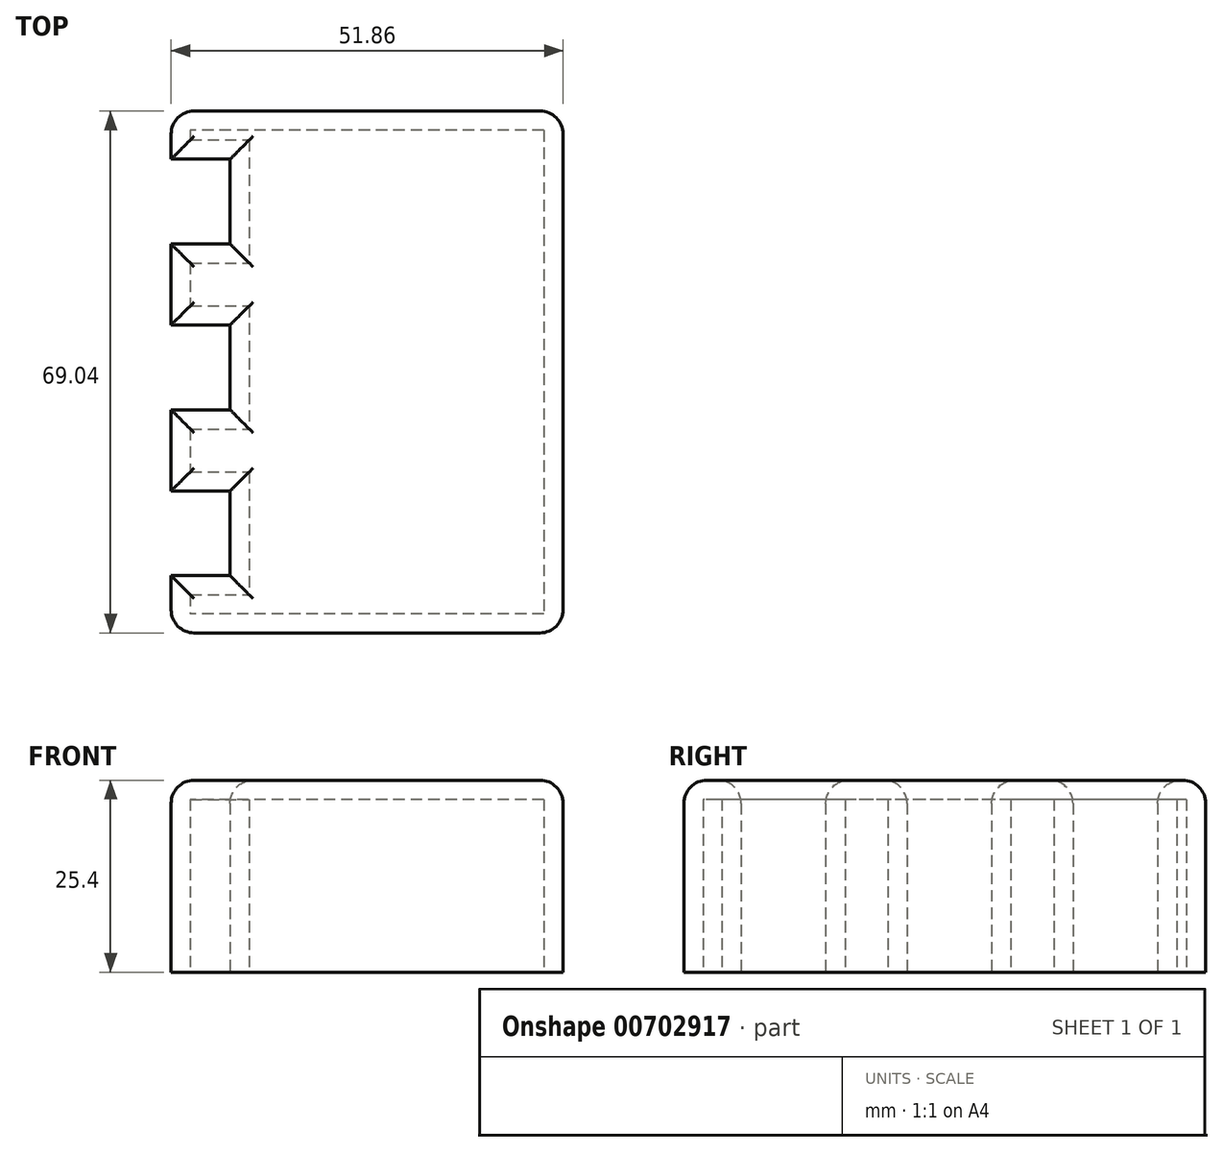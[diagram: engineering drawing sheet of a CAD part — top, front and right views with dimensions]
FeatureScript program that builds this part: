
annotation { "Feature Type Name" : "Feature", "Feature Type Description" : "" }
export const myFeature = defineFeature(function(context is Context, id is Id, definition is map)
    precondition{}
    {
        {
            var Q0;
            Q0=qCreatedBy(makeId("Top.planeOp"),FACE);
            var sketch = newSketch(context, id + "F0", { "sketchPlane" : qUnion([Q0])});
            skLineSegment(sketch, "E0.bottom", {"start": v(25.93, 34.52) * mm, "end": v(-25.93, 34.52) * mm});
            skLineSegment(sketch, "E0.top", {"start": v(25.93, -34.52) * mm, "end": v(-25.93, -34.52) * mm});
            skLineSegment(sketch, "E0.left", {"start": v(25.93, 34.52) * mm, "end": v(25.93, -34.52) * mm});
            skLineSegment(sketch, "E0.right", {"start": v(-25.93, 34.52) * mm, "end": v(-25.93, 28.16) * mm});
            skPoint(sketch, "E0.middle", {"position": v(0, 0) * mm});
            skLineSegment(sketch, "E1.bottom", {"start": v(-25.93, 28.16) * mm, "end": v(-18.13, 28.16) * mm});
            skLineSegment(sketch, "E1.top", {"start": v(-25.93, 16.96) * mm, "end": v(-18.13, 16.96) * mm});
            skLineSegment(sketch, "E1.right", {"start": v(-18.13, 28.16) * mm, "end": v(-18.13, 16.96) * mm});
            skLineSegment(sketch, "E2.bottom", {"start": v(-25.93, 6.2) * mm, "end": v(-18.13, 6.2) * mm});
            skLineSegment(sketch, "E2.top", {"start": v(-25.93, -5) * mm, "end": v(-18.13, -5) * mm});
            skLineSegment(sketch, "E2.right", {"start": v(-18.13, 6.2) * mm, "end": v(-18.13, -5) * mm});
            skLineSegment(sketch, "E3.bottom", {"start": v(-25.93, -15.75) * mm, "end": v(-18.13, -15.75) * mm});
            skLineSegment(sketch, "E3.top", {"start": v(-25.93, -26.95) * mm, "end": v(-18.13, -26.95) * mm});
            skLineSegment(sketch, "E3.right", {"start": v(-18.13, -15.75) * mm, "end": v(-18.13, -26.95) * mm});
            skLineSegment(sketch, "E4.trimOffspring", {"start": v(-25.93, 16.96) * mm, "end": v(-25.93, 6.2) * mm});
            skLineSegment(sketch, "E5.trimOffspring", {"start": v(-25.93, -5) * mm, "end": v(-25.93, -15.75) * mm});
            skLineSegment(sketch, "E6.trimOffspring", {"start": v(-25.93, -26.95) * mm, "end": v(-25.93, -34.52) * mm});
            skSolve(sketch);
        }
        {
            var Q0;
            Q0 = qSketchRegion(id + "F0", true);
            extrude(context, id + "F1", {"entities" : qUnion([Q0]), "endBound" : BoundingType.SYMMETRIC, "depth" : 25.4 * mm, "offsetDistance" : 25.4 * mm});
        }
        {
            var Q0;
            Q0=makeQuery(id+"F1.opExtrude","CAP_FACE",FACE,{"disambiguationData":[OSD([sQuery(id+"F0.wireOp",EDGE,"E0.bottom"),sQuery(id+"F0.wireOp",EDGE,"E0.top"),sQuery(id+"F0.wireOp",EDGE,"E0.left"),sQuery(id+"F0.wireOp",EDGE,"E0.right"),sQuery(id+"F0.wireOp",EDGE,"E1.bottom"),sQuery(id+"F0.wireOp",EDGE,"E1.top"),sQuery(id+"F0.wireOp",EDGE,"E1.right"),sQuery(id+"F0.wireOp",EDGE,"E2.bottom"),sQuery(id+"F0.wireOp",EDGE,"E2.top"),sQuery(id+"F0.wireOp",EDGE,"E2.right"),sQuery(id+"F0.wireOp",EDGE,"E3.bottom"),sQuery(id+"F0.wireOp",EDGE,"E3.top"),sQuery(id+"F0.wireOp",EDGE,"E3.right"),sQuery(id+"F0.wireOp",EDGE,"E4.trimOffspring"),sQuery(id+"F0.wireOp",EDGE,"E5.trimOffspring"),sQuery(id+"F0.wireOp",EDGE,"E6.trimOffspring")])],"isStart":true});
            var Q1;
            Q1=makeQuery(id+"F1.opExtrude","SWEPT_BODY",BODY,{"disambiguationData":[OSD([sQuery(id+"F0.wireOp",EDGE,"E0.bottom"),sQuery(id+"F0.wireOp",EDGE,"E0.top"),sQuery(id+"F0.wireOp",EDGE,"E0.left"),sQuery(id+"F0.wireOp",EDGE,"E0.right"),sQuery(id+"F0.wireOp",EDGE,"E1.bottom"),sQuery(id+"F0.wireOp",EDGE,"E1.top"),sQuery(id+"F0.wireOp",EDGE,"E1.right"),sQuery(id+"F0.wireOp",EDGE,"E2.bottom"),sQuery(id+"F0.wireOp",EDGE,"E2.top"),sQuery(id+"F0.wireOp",EDGE,"E2.right"),sQuery(id+"F0.wireOp",EDGE,"E3.bottom"),sQuery(id+"F0.wireOp",EDGE,"E3.top"),sQuery(id+"F0.wireOp",EDGE,"E3.right"),sQuery(id+"F0.wireOp",EDGE,"E4.trimOffspring"),sQuery(id+"F0.wireOp",EDGE,"E5.trimOffspring"),sQuery(id+"F0.wireOp",EDGE,"E6.trimOffspring")])]});
            shell(context, id + "F2", {"entities" : qUnion([Q0]), "parts" : qUnion([Q1]), "thickness" : 2.54 * mm});
        }
        {
            var Q0;
            Q0=makeQuery(id+"F1.opExtrude","CAP_EDGE",EDGE,{"disambiguationData":[OSD([sQuery(id+"F0.wireOp",EDGE,"E0.left")])],"isStart":false});
            var Q1;
            Q1=makeQuery(id+"F1.opExtrude","CAP_EDGE",EDGE,{"disambiguationData":[OSD([sQuery(id+"F0.wireOp",EDGE,"E0.bottom")])],"isStart":false});
            var Q2;
            Q2=makeQuery(id+"F1.opExtrude","CAP_EDGE",EDGE,{"disambiguationData":[OSD([sQuery(id+"F0.wireOp",EDGE,"E0.right")])],"isStart":false});
            var Q3;
            Q3=makeQuery(id+"F1.opExtrude","CAP_EDGE",EDGE,{"disambiguationData":[OSD([sQuery(id+"F0.wireOp",EDGE,"E1.right")])],"isStart":false});
            var Q4;
            Q4=makeQuery(id+"F1.opExtrude","CAP_EDGE",EDGE,{"disambiguationData":[OSD([sQuery(id+"F0.wireOp",EDGE,"E1.top")])],"isStart":false});
            var Q5;
            Q5=makeQuery(id+"F1.opExtrude","CAP_EDGE",EDGE,{"disambiguationData":[OSD([sQuery(id+"F0.wireOp",EDGE,"E4.trimOffspring")])],"isStart":false});
            var Q6;
            Q6=makeQuery(id+"F1.opExtrude","CAP_EDGE",EDGE,{"disambiguationData":[OSD([sQuery(id+"F0.wireOp",EDGE,"E2.bottom")])],"isStart":false});
            var Q7;
            Q7=makeQuery(id+"F1.opExtrude","CAP_EDGE",EDGE,{"disambiguationData":[OSD([sQuery(id+"F0.wireOp",EDGE,"E2.right")])],"isStart":false});
            var Q8;
            Q8=makeQuery(id+"F1.opExtrude","CAP_EDGE",EDGE,{"disambiguationData":[OSD([sQuery(id+"F0.wireOp",EDGE,"E2.top")])],"isStart":false});
            var Q9;
            Q9=makeQuery(id+"F1.opExtrude","CAP_EDGE",EDGE,{"disambiguationData":[OSD([sQuery(id+"F0.wireOp",EDGE,"E5.trimOffspring")])],"isStart":false});
            var Q10;
            Q10=makeQuery(id+"F1.opExtrude","CAP_EDGE",EDGE,{"disambiguationData":[OSD([sQuery(id+"F0.wireOp",EDGE,"E3.bottom")])],"isStart":false});
            var Q11;
            Q11=makeQuery(id+"F1.opExtrude","CAP_EDGE",EDGE,{"disambiguationData":[OSD([sQuery(id+"F0.wireOp",EDGE,"E3.right")])],"isStart":false});
            var Q12;
            Q12=makeQuery(id+"F1.opExtrude","CAP_EDGE",EDGE,{"disambiguationData":[OSD([sQuery(id+"F0.wireOp",EDGE,"E3.top")])],"isStart":false});
            var Q13;
            Q13=makeQuery(id+"F1.opExtrude","CAP_EDGE",EDGE,{"disambiguationData":[OSD([sQuery(id+"F0.wireOp",EDGE,"E6.trimOffspring")])],"isStart":false});
            var Q14;
            Q14=makeQuery(id+"F1.opExtrude","CAP_EDGE",EDGE,{"disambiguationData":[OSD([sQuery(id+"F0.wireOp",EDGE,"E0.top")])],"isStart":false});
            var Q15;
            Q15=makeQuery(id+"F1.opExtrude","CAP_EDGE",EDGE,{"disambiguationData":[OSD([sQuery(id+"F0.wireOp",EDGE,"E1.bottom")])],"isStart":false});
            var Q16;
            Q16=makeQuery(id+"F1.opExtrude","SWEPT_EDGE",EDGE,{"disambiguationData":[OSD([sQuery(id+"F0.wireOp",EDGE,"E0.top"),sQuery(id+"F0.wireOp",EDGE,"E6.trimOffspring")])]});
            var Q17;
            Q17=makeQuery(id+"F1.opExtrude","SWEPT_EDGE",EDGE,{"disambiguationData":[OSD([sQuery(id+"F0.wireOp",EDGE,"E0.top"),sQuery(id+"F0.wireOp",EDGE,"E0.left")])]});
            var Q18;
            Q18=makeQuery(id+"F1.opExtrude","SWEPT_EDGE",EDGE,{"disambiguationData":[OSD([sQuery(id+"F0.wireOp",EDGE,"E0.bottom"),sQuery(id+"F0.wireOp",EDGE,"E0.left")])]});
            var Q19;
            Q19=makeQuery(id+"F1.opExtrude","SWEPT_EDGE",EDGE,{"disambiguationData":[OSD([sQuery(id+"F0.wireOp",EDGE,"E0.bottom"),sQuery(id+"F0.wireOp",EDGE,"E0.right")])]});
            fillet(context, id + "F3", {"entities" : qUnion([Q0, Q1, Q2, Q3, Q4, Q5, Q6, Q7, Q8, Q9, Q10, Q11, Q12, Q13, Q14, Q15, Q16, Q17, Q18, Q19]), "radius" : 3.05 * mm, "tangentPropagation" : true, "allowEdgeOverflow" : false});
        }
    });
